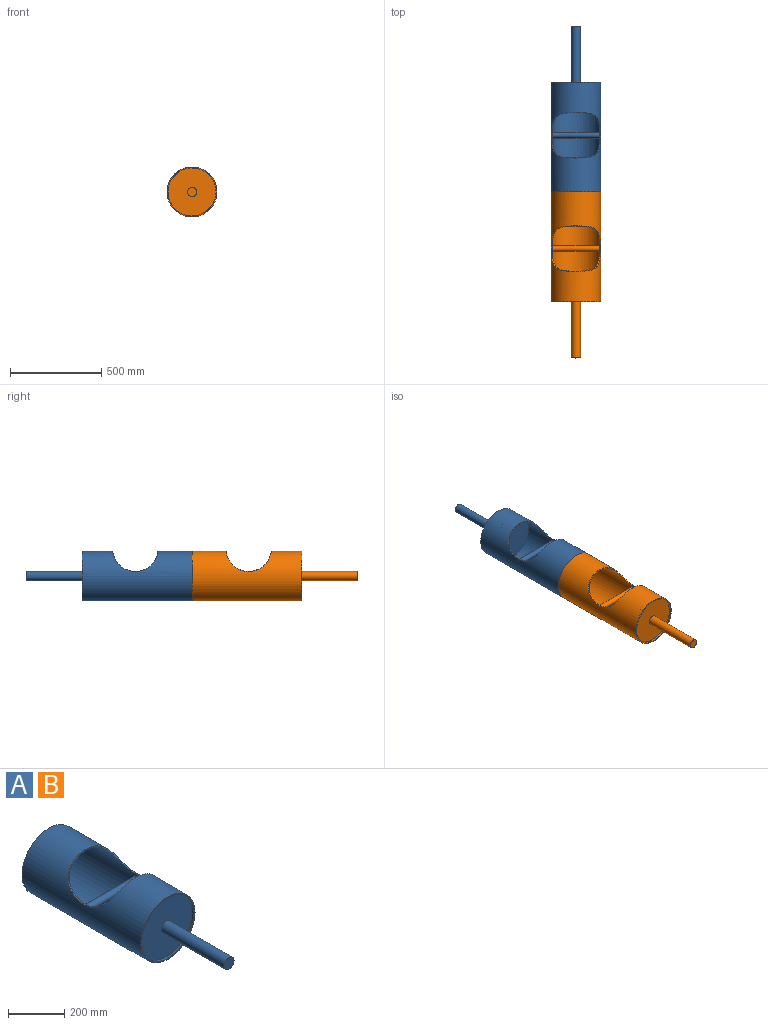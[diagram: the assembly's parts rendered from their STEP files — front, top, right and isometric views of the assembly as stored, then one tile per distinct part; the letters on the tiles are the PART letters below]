
ASSEMBLY  parts=2 mates=1
PART A: 15 faces, bbox 273x908x273 mm
  f0: cylinder r=131.5mm len=500mm, axis (0,1,0), area 336598.4mm2, adj f4,f5,f6,f7
  f1: cylinder r=136.5mm len=600mm, axis (0,1,0), area 435166.7mm2, adj f3,f4,f7
  f2: cylinder r=131.5mm len=263mm, axis (0,1,0), area 8262.4mm2, adj f3,f8
  f3: plane 273x273mm, normal (0,-1,0), area 4209.7mm2, adj f1,f2
  f4: plane 273x273mm, normal (0,1,0), area 4209.7mm2, adj f0,f1
  f5: plane 263x263mm, normal (0,1,0), area 54325.2mm2, adj f0
  f6: cylinder r=15mm len=263mm, axis (-1,0,0), area 24706.4mm2, adj f0
  f7: cylinder r=125mm len=268.38mm, axis (1,0,0), area 5227.7mm2, adj f0,f1
  f8: plane 263x263mm, normal (0,-1,0), area 52361.7mm2, adj f2,f10
  f9: plane 50x50mm, normal (0,-1,0), area 1963.5mm2, adj f10
  f10: cylinder r=25mm len=318mm, axis (0,1,0), area 49951.3mm2, adj f8,f9
  f11: cylinder r=25mm len=74mm, axis (0,1,0), area 11623.9mm2, adj f12,f14
  f12: plane 263x263mm, normal (0,-1,0), area 52361.7mm2, adj f11,f13
  f13: cylinder r=131.5mm len=263mm, axis (0,1,0), area 61141.7mm2, adj f12,f14
  f14: plane 263x263mm, normal (0,1,0), area 52361.7mm2, adj f11,f13
PART B: same geometry as A
PLACE A rot(axis=(0,0,1),180deg) t=(-288.7,151.74,-180.86)mm
PLACE B t=(-288.7,151.74,-180.86)mm
MATE slider A.f0 <-> B.f0  axis (0,-1,0) through (-288.7,151.74,-180.86)mm
